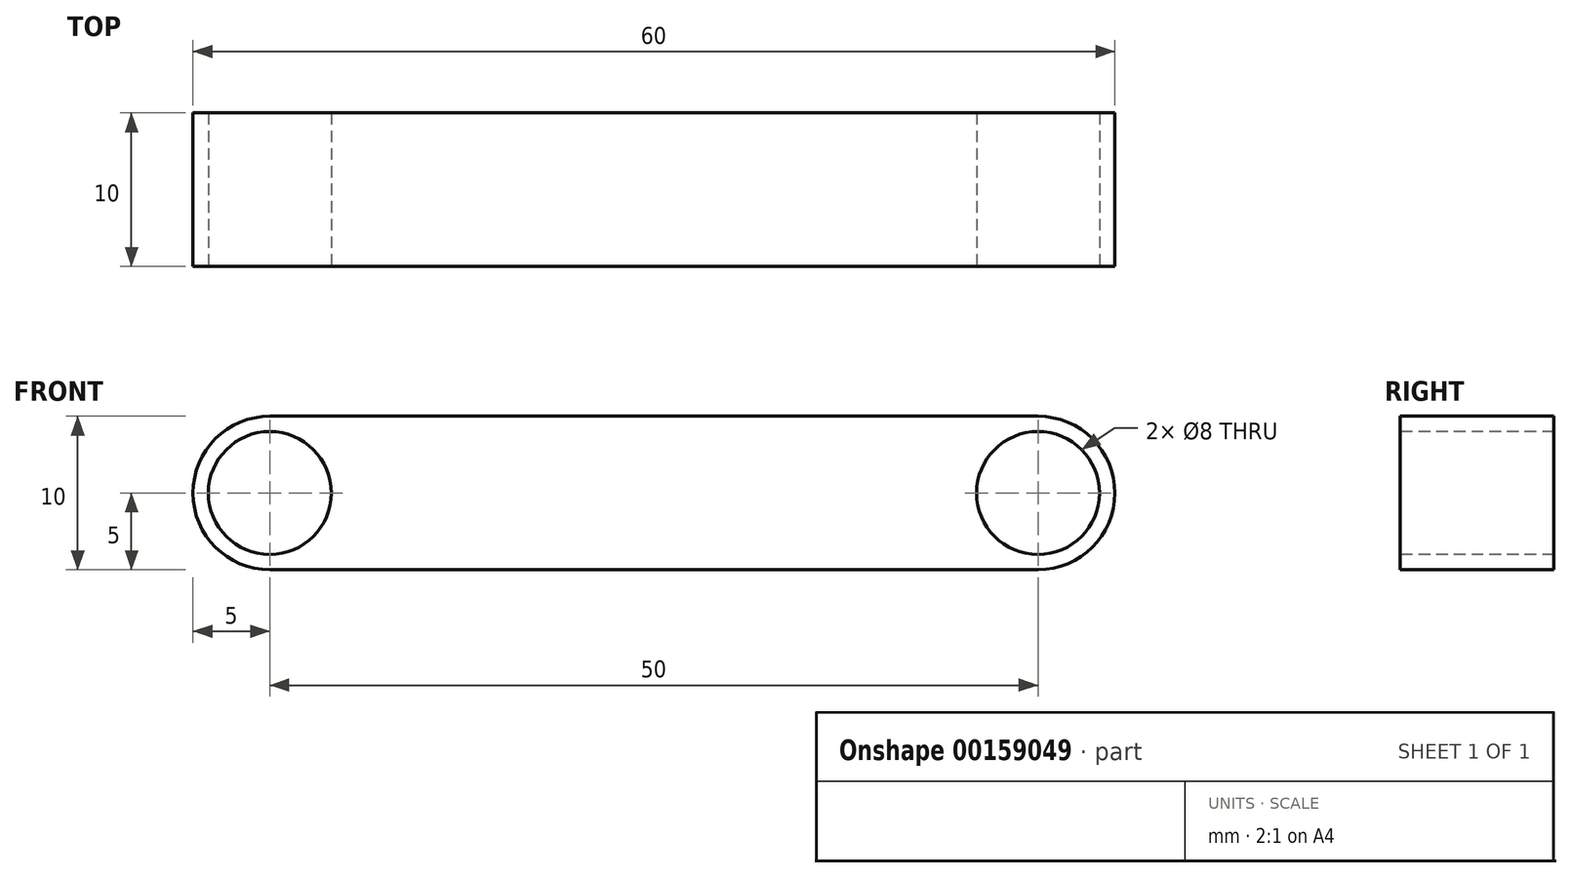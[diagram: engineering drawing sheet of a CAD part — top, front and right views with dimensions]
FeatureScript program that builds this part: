
annotation { "Feature Type Name" : "Feature", "Feature Type Description" : "" }
export const myFeature = defineFeature(function(context is Context, id is Id, definition is map)
    precondition{}
    {
        {
            var Q0;
            Q0=qCreatedBy(makeId("Top.planeOp"),FACE);
            var sketch = newSketch(context, id + "F0", { "sketchPlane" : qUnion([Q0])});
            skLineSegment(sketch, "E0.bottom", {"start": v(-30, 5) * mm, "end": v(30, 5) * mm});
            skLineSegment(sketch, "E0.top", {"start": v(-30, -5) * mm, "end": v(30, -5) * mm});
            skLineSegment(sketch, "E0.left", {"start": v(-30, 5) * mm, "end": v(-30, -5) * mm});
            skLineSegment(sketch, "E0.right", {"start": v(30, 5) * mm, "end": v(30, -5) * mm});
            skPoint(sketch, "E0.middle", {"position": v(0, 0) * mm});
            skSolve(sketch);
        }
        {
            var Q0;
            Q0 = qSketchRegion(id + "F0", true);
            extrude(context, id + "F1", {"entities" : qUnion([Q0]), "depth" : 10 * mm});
        }
        {
            var Q0;
            Q0=makeQuery(id+"F1.opExtrude","SWEPT_FACE",FACE,{"disambiguationData":[OSD([sQuery(id+"F0.wireOp",EDGE,"E0.top")])]});
            var sketch = newSketch(context, id + "F2", { "sketchPlane" : qUnion([Q0])});
            skCircle(sketch, "E1", {"center": v(-25, 5) * mm, "radius": 4 * mm});
            skCircle(sketch, "E2.MirrorC", {"center": v(25, 5) * mm, "radius": 4 * mm});
            skSolve(sketch);
        }
        {
            var Q0;
            Q0 = qSketchRegion(id + "F2", true);
            extrude(context, id + "F3", {"entities" : qUnion([Q0]), "operationType" : NewBodyOperationType.REMOVE, "endBound" : BoundingType.THROUGH_ALL, "oppositeDirection" : true, "depth" : 25 * mm});
        }
        {
            var Q0;
            Q0=makeQuery(id+"F1.opExtrude","CAP_EDGE",EDGE,{"disambiguationData":[OSD([sQuery(id+"F0.wireOp",EDGE,"E0.left")])],"isStart":false});
            var Q1;
            Q1=makeQuery(id+"F1.opExtrude","CAP_EDGE",EDGE,{"disambiguationData":[OSD([sQuery(id+"F0.wireOp",EDGE,"E0.left")])],"isStart":true});
            var Q2;
            Q2=makeQuery(id+"F1.opExtrude","CAP_EDGE",EDGE,{"disambiguationData":[OSD([sQuery(id+"F0.wireOp",EDGE,"E0.right")])],"isStart":false});
            var Q3;
            Q3=makeQuery(id+"F1.opExtrude","CAP_EDGE",EDGE,{"disambiguationData":[OSD([sQuery(id+"F0.wireOp",EDGE,"E0.right")])],"isStart":true});
            fillet(context, id + "F4", {"entities" : qUnion([Q0, Q1, Q2, Q3]), "radius" : 5 * mm, "tangentPropagation" : true, "allowEdgeOverflow" : false});
        }
        {
            var Q0;
            Q0=makeQuery(id+"F1.opExtrude","SWEPT_FACE",FACE,{"disambiguationData":[OSD([sQuery(id+"F0.wireOp",EDGE,"E0.top")])]});
            var sketch = newSketch(context, id + "F5", { "sketchPlane" : qUnion([Q0])});
            skCircle(sketch, "E3", {"center": v(45, 5) * mm, "radius": 4 * mm});
            skSolve(sketch);
        }
        {
            var Q0;
            Q0 = qSketchRegion(id + "F5", true);
            extrude(context, id + "F6", {"entities" : qUnion([Q0]), "operationType" : NewBodyOperationType.REMOVE, "endBound" : BoundingType.THROUGH_ALL, "oppositeDirection" : true, "depth" : 25 * mm});
        }
    });
